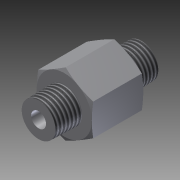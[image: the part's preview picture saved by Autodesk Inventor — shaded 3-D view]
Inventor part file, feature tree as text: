
AUTODESK INVENTOR PART (.ipt)
format: ipt  version: 2016 SP1 (Build 200210100, 210)  size: 143,872 bytes
history: native  units: in
note: dims shown in document units (in); Inventor stores cm internally (conversion verified against a paired STEP export)
features: sketch x4, extrude x3, plane x2, thread x2, other x1, hole x1, revolve x1, mirror x1, reference x1
ambient origin geometry x8: Origin, YZ Plane, XZ Plane, XY Plane, X Axis, Y Axis, Z Axis, Center Point
bodies: Solid1 (feature_tree)
feature tree (16):
  sketch  "Sketch1"  dims[d2=0.5in d3=0.0in d20=0.25in d21=-0.0123in]
  extrude  "Extrusion1"  Depth=0.25in
  plane  "Work Plane1"
  other  "Work Axis3"
  extrude  "Extrusion3"  Depth=0.25in
  thread  "Thread2"  [1 undecoded]
  hole  "Hole2"  [1 undecoded]
  extrude  "Extrusion4"  Depth=0.0414in
  thread  "Thread3"  [1 undecoded]
  revolve  "Revolution3"  [1 undecoded]
  plane  "Work Plane4"
  mirror  "Mirror4"
  sketch  "Sketch6"  dims[d22=0.392in d23=0.0in]
  reference  "Reference3"
  sketch  "Sketch7"  dims[d24=0.13in d25=0.75in d26=0.375in d27=0.25in d28=0.5635in d29=1.0in d30=0.8108in d31=0.25in d32=-0.0123in d33=0.392in d34=0.0in]
  sketch  "Sketch8"  dims[d35=90.0deg d36=0.5355in d37=0.0414in d38=0.0415in]
note: 4 required parameter values undecoded (feature->parameter linkage not recoverable at this tier; creation-order binding heuristic only, values carry confidence <= 0.55)
